# Revit family: Power-ModularDevices-GEWISS-90AM-CHANGE_OVER_SWITCH
name_source: partatom
category: Apparecchi elettrici
revit_build: Autodesk Revit 2016 (Build: 20161004_0715(x64)
units: mm (PartAtom-declared; Revit-internal decimal feet)

## family parameters
Condiviso = No
Host = Superficie
Mantenere orientamento annotazione = Sì
Numero OmniClass = 23.80.30.00
Punto di calcolo locali = Sì
Quota connettore circolare = Usa diametro
Taglio con vuoti quando caricato = No
Tipo di parte = Normale
Titolo OmniClass = Distribution Devices

## types (6) — shared parameters
A = 18 mm  [stored 0.0590551 ft]
B = 85 mm  [stored 0.278871 ft]
C = 65 mm  [stored 0.213255 ft]
Catalogue = POWER
Catalogue Range = 90 AM
D = 45 mm  [stored 0.147638 ft]
Electrocod = 0130
Fin_Amperometro = <Per categoria>
IDF = c3217e07-725f-4088-abf0-96e09acf5209
IDT = f5c7732d-d936-4eb1-8972-ea14e90c1cbf
Immagine tipo = GW96556.jpg
No. Chorus modules = 1
Numero poli = 2
Potenza in Watt = 0 V
Produttore = GEWISS S.p.A.
Prospetto di default = 1219 mm
Rated voltage = 250V
Technical sheet = https://www.gewiss.com
URL = https://www.gewiss.com
Version file RFA = 18.0

## per-type parameters (varying)
| type | Descrizione | EAN code | Modello | Number of poles | Rated current (In) | Type |
| GW96551 - CHANGE OVER SWITCH (1-2) 16A 1P 250V 1M | CHANGE OVER SWITCH (1-2) 16A 1P 250V 1M | 8011564447752 | GW96551 | 1P | 16A | Change-over switch (1-2) |
| GW96556 - TWO-WAY-SWITCH (1-2) 2P 16A 250V 1M | TWO-WAY-SWITCH (1-2) 2P 16A 250V 1M | 8011564447943 | GW96556 | 2P (1NO+1NC) | 32A | Two-ways switch (1-2) |
| GW96552 - CHANGE OVER SWITCH (1-2) 16A 2P 250V 1M | CHANGE OVER SWITCH (1-2) 16A 2P 250V 1M | 8011564447929 | GW96552 | 2P | 16A | Change-over switch (1-2) |
| GW96553 - THREE-WAY-SWITCH (1-0-2) 1P 16A 250V 1M | THREE-WAY-SWITCH (1-0-2) 1P 16A 250V 1M | 8011564447769 | GW96553 | 1P | 16A | Three-way  switch (1-0-2) |
| GW96554 - THREE-WAY-SWITCH (1-0-2) 2P 16A 250V 1M | THREE-WAY-SWITCH (1-0-2) 2P 16A 250V 1M | 8011564447936 | GW96554 | 2P | 16A | Three-way  switch (1-0-2) |
| GW96555 - TWO-WAY-SWITCH (1-2) 1P 16A 250V 1M | TWO-WAY-SWITCH (1-2) 1P 16A 250V 1M | 8011564447776 | GW96555 | 2P (1NO+1NC) | 16A | Two-ways switch (1-2) |

note: [stored X ft] marks values corroborated as IEEE doubles in the binary element streams (Revit-internal decimal feet)
